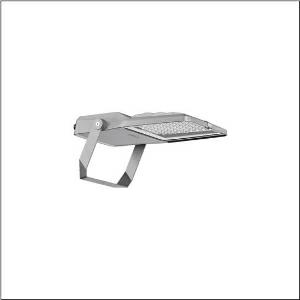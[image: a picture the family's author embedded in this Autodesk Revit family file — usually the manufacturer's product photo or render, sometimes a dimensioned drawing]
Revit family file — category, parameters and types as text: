
# Revit family: floodlight_fl_21_iq_mini___pl33t_5xa7772b5f1a_9cd7
name_source: partatom
category: Lighting Fixtures
units: mm (PartAtom-declared; Revit-internal decimal feet)

## family parameters
Cut with Voids When Loaded = No
Host = Face
Light Source = No
Part Type = Normal
Room Calculation Point = No
Round Connector Dimension = Use Diameter
Shared = No

## types (1)
- --- (1 x LED, 5750 lm, 45.5 W, 4000K)
    Apparent Load = 46 VA
    CIE Flux Codes = 26 75 99 100 100
    Color Rendering = 80
    Color Temperature = 4000K
    Default Elevation = 1800 mm
    Description = Floodlight FL 21 iQ mini, floodlight, primary light control with lens, of PMMA, primary optical cover: protective disc, of toughened safety glass, transparent, light distribution: PL33T, light emission: direct distribution, installation type: surface-mounted, LED, High Power LED, rated luminous flux: 5.750lm, luminous efficacy: 126lm/W, light colour: 840, colour temperature: 4000K, control gear: iQ Street-Remote/DALI, control: Street-Remote, Auto-Match, Temp-Guard, Night-Set, Smart-Wire, Desk-Remote (wireless, voltage-free reading and setting of iQ features in the workshop via application-optimized NFC function/RFID function), optimised constant luminous flux control (CLO 2.0), with terminal, 6-pole, mains connection: 220..240V, AC, 50/60Hz, start of lifetime: 46W, end of service life: 48W, reduction: 22W, luminaire housing, of diecast aluminium, powder-coated, Siteco® metallic grey (DB 702S), corrosivity category C5 mid according to DIN EN ISO 12944, suitable for swimming pools, chlorine-resistant, sealing non-destructively replaceable, mounting bracket, of steel, galvanised, powder-coated, Siteco® metallic grey (DB 702S), protection rating (complete): IP66, insulation class (complete): insulation class II (safety insulation), certification: CE, ENEC, VDE, protection symbol: D, impact resistance: IK08, permissible operating ambient temperature: -40..+40°C, permissible operating ambient temperature for outdoor applications: -40..+50°C, standard: DIN EN 12944, LABS conformity tested according to VDMA 24364:2018-05, packaging unit: 1 piece

Light Distribution: PL33T
    Height = 70 mm
    Lamp = 1 x LED
    Lamp Light Flux = 5750 lm
    Lamp Power = 45.5 W
    Lamp count = 1
    Length = 485 mm
    Luminous efficacy = 126 lm/W
    Manufacturer = Siteco
    ModVariant = No
    Model = 5XA7772B5F1A
    Number of Poles = 1
    OnlyDefault = Yes
    Power Factor = 1
    Product Name = Floodlight FL 21 iQ mini | PL33T
    Product group = floodlight | pylon annexe
    ProductGroupID = 6200
    Protection Class = Protection class II
    Protection Degree = IP 66
    RLX_Detail_Level = 1
    RLX_Emergency_Light_Flux = 0 lm
    RLX_Emergency_Type = 0
    RLX_Emergency_Type_DB = No
    RlxData = <blob elided: 96121 chars, md5=4975c111>
    Socket = socket
    Standby Power = 0 W
    System Light Flux = 5750 lm
    System Power = 46 W
    Type Comments = factory setting: luminous flux: 100 % | dim-lin: 254 | 463 mA
    Type Image = l_1006845.jpg
    URL = http://relux.com
    VarID = @adj_149852
    Voltage = 0 V
    Weight = 0.00 kg
    Width = 337 mm

## geometry (parser evidence)
native form markers: Blend x4, Sweep x13
no freeform markers — native parametric forms only
